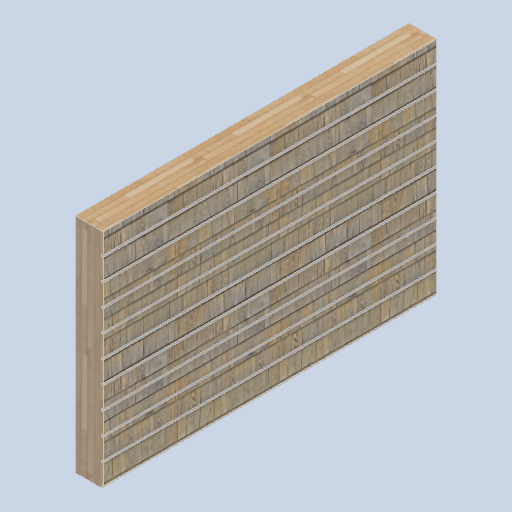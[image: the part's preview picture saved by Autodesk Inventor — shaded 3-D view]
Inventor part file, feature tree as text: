
AUTODESK INVENTOR PART (.ipt)
format: ipt  version: 2024.2 (Build 282272000, 272)  size: 368,640 bytes
history: native  units: in
note: dims shown in document units (in); Inventor stores cm internally (conversion verified against a paired STEP export)
features: other x3, sketch x1
ambient origin geometry x8: Origin, YZ Plane, XZ Plane, XY Plane, X Axis, Y Axis, Z Axis, Center Point
bodies: Solid1 (feature_tree)
feature tree (4):
  other  "side_wall_block_01.ipt"
  other  "Solid1::side_wall_block_01.ipt"
  other  "TaggingFeature1"
  sketch  "Sketch1"  dims[d0=0.3937in]
